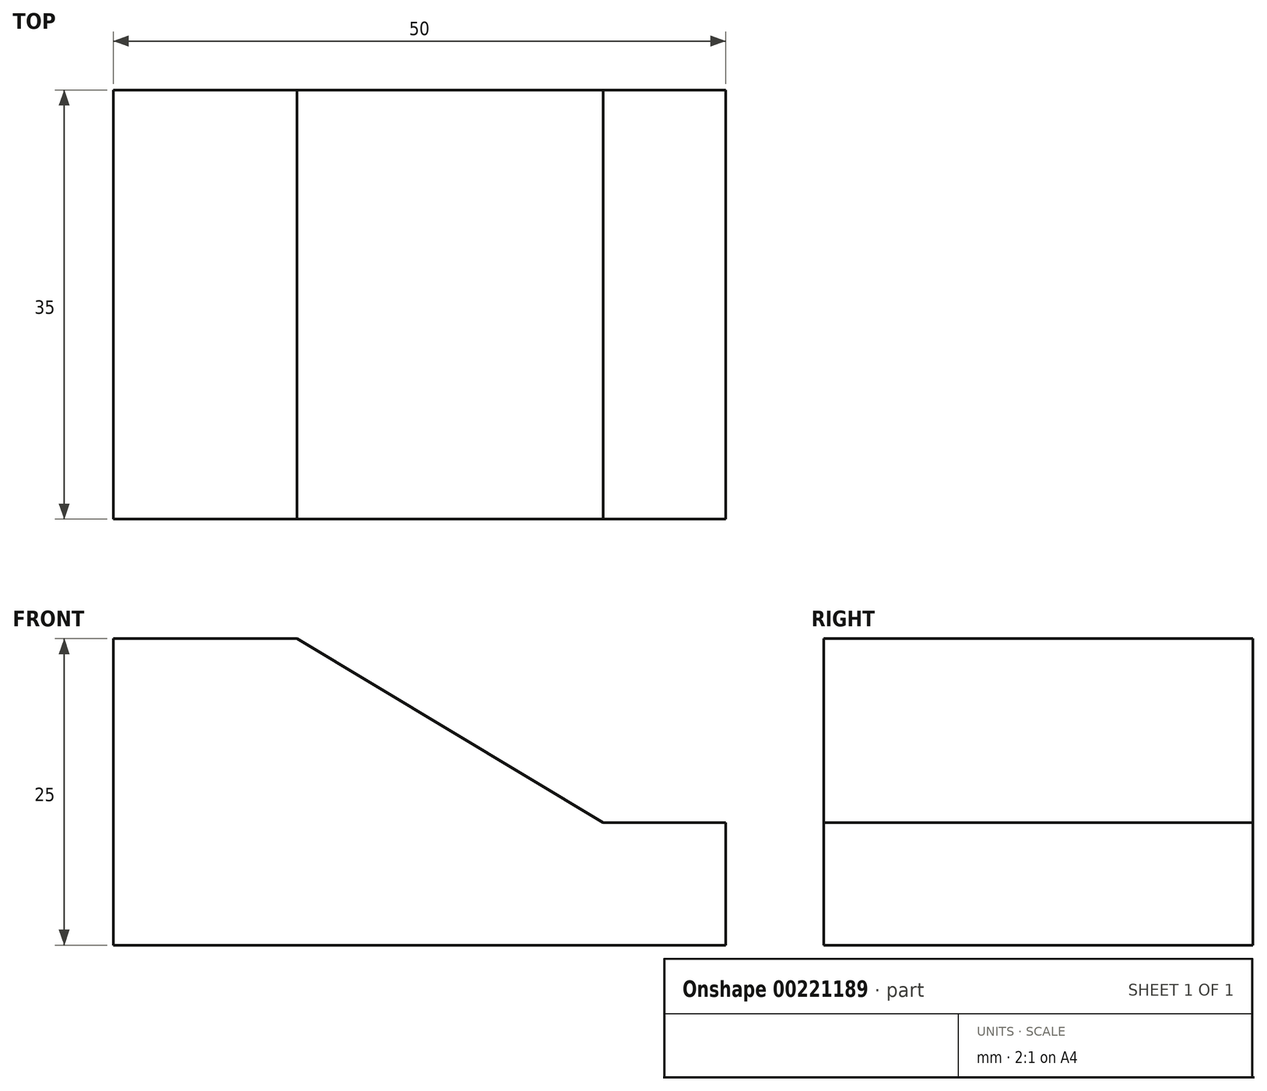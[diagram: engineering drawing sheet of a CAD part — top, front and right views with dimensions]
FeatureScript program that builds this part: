
annotation { "Feature Type Name" : "Feature", "Feature Type Description" : "" }
export const myFeature = defineFeature(function(context is Context, id is Id, definition is map)
    precondition{}
    {
        {
            var Q0;
            Q0=qCreatedBy(makeId("Front.planeOp"),FACE);
            var sketch = newSketch(context, id + "F0", { "sketchPlane" : qUnion([Q0])});
            skLineSegment(sketch, "E0", {"start": v(0, 0) * mm, "end": v(0, 25) * mm});
            skLineSegment(sketch, "E1", {"start": v(0, 25) * mm, "end": v(15, 25) * mm});
            skLineSegment(sketch, "E2", {"start": v(15, 25) * mm, "end": v(40, 10) * mm});
            skLineSegment(sketch, "E3", {"start": v(40, 10) * mm, "end": v(50, 10) * mm});
            skLineSegment(sketch, "E4", {"start": v(50, 10) * mm, "end": v(50, 0) * mm});
            skLineSegment(sketch, "E5", {"start": v(50, 0) * mm, "end": v(0, 0) * mm});
            skSolve(sketch);
        }
        {
            var Q0;
            Q0=makeQuery(id+"F0.imprint","IMPRINT",FACE,{"disambiguationData":[TD([[makeQuery(id+"F0.imprint","IMPRINT",EDGE,{"derivedFrom":sQuery(id+"F0.wireOp",EDGE,"E0")}),-1.0]])]});
            extrude(context, id + "F1", {"entities" : qUnion([Q0]), "endBound" : BoundingType.SYMMETRIC, "depth" : 35 * mm});
        }
    });
